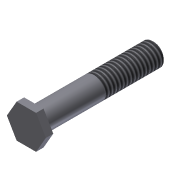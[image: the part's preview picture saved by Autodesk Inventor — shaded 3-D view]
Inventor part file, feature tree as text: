
AUTODESK INVENTOR PART (.ipt)
format: ipt  version: 2011 (Build 150239000, 239)  size: 95,232 bytes
history: native  units: in
note: dims shown in document units (in); Inventor stores cm internally (conversion verified against a paired STEP export)
features: extrude x2, sketch x2, thread x1, chamfer x1
ambient origin geometry x8: Origin, YZ Plane, XZ Plane, XY Plane, X Axis, Y Axis, Z Axis, Center Point
bodies: Solid1 (feature_tree)
feature tree (6):
  extrude  "Extrusion1"  Depth=2.0in TaperAngle=0.0deg
  extrude  "Extrusion2"  Depth=0.125in TaperAngle=0.0deg
  thread  "Thread1"  [1 undecoded]
  chamfer  "Chamfer1"  Distance=0.02in Angle=45.0deg
  sketch  "Sketch1"  dims[d0=0.375in d1=2.0in d2=0.0in]
  sketch  "Sketch2"  dims[d3=0.5625in d4=0.125in d5=0.0in d6=1.0in d7=0.0in d8=0.02in d9=0.125in d10=45.0deg]
note: 1 required parameter value undecoded (feature->parameter linkage not recoverable at this tier; creation-order binding heuristic only, values carry confidence <= 0.55)
